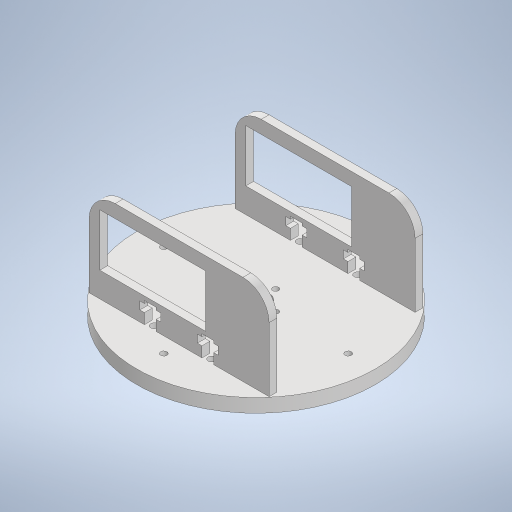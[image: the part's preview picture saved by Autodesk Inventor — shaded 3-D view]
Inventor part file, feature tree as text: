
AUTODESK INVENTOR PART (.ipt)
format: ipt  version: 2023 (Build 270158000, 158)  size: 415,744 bytes
history: native  units: mm
features: extrude x11, sketch x11, pattern_circular x2, mirror x2, other x1, fillet x1
ambient origin geometry x8: Origin, YZ Plane, XZ Plane, XY Plane, X Axis, Y Axis, Z Axis, Center Point
bodies: Body1 (feature_tree)
feature tree (28):
  other  "Sólido1"
  extrude  "Extrusión1"  Depth=5.2mm TaperAngle=0.0deg
  extrude  "Extrusión2"  Depth=2.46mm
  pattern_circular  "Patrón circular1"  Count=4 Angle=360.0deg
  extrude  "Extrusión3"  Depth=11.0mm
  extrude  "Extrusión4"  Depth=7.2mm
  extrude  "Extrusión5"  Depth=2.8mm
  fillet  "Empalme1"  Radius=2.8mm
  extrude  "Extrusión6"  Depth=68.8mm
  mirror  "Simetría1"
  mirror  "Simetría2"
  extrude  "Extrusión7"  Depth=3.0mm TaperAngle=0.0deg
  extrude  "Extrusión8"  Depth=10.0mm
  pattern_circular  "Patrón circular2"  [2 undecoded]
  extrude  "Extrusión9"  Depth=10.0mm
  extrude  "Extrusión10"  Depth=10.0mm TaperAngle=0.0deg
  extrude  "Extrusión11"  Depth=10.0mm
  sketch  "Boceto1"  dims[d0=91.1mm d1=5.2mm d2=0.0mm]
  sketch  "Boceto2"  dims[d3=70.5mm d4=2.46mm]
  sketch  "Boceto3"  dims[d5=5.2mm d6=0.0mm d7=40.0mm d8=360.0deg]
  sketch  "Boceto4"  dims[d11=27.9mm d12=11.0mm]
  sketch  "Boceto5"  dims[d13=7.2mm d14=7.2mm]
  sketch  "Boceto6"  dims[d15=2.6mm d16=0.0mm d17=2.8mm d18=2.8mm]
  sketch  "Boceto7"  dims[d19=2.6mm d20=0.0mm d21=68.8mm]
  sketch  "Boceto8"  dims[d22=3.0mm d23=34.5mm d24=0.0mm]
  sketch  "Boceto9"  dims[d25=10.0mm d26=8.0mm]
  sketch  "Boceto10"  dims[d27=4.5mm]
  sketch  "Boceto11"  dims[d28=3.0mm d29=7.0mm d30=8.0mm d31=34.5mm d32=0.0mm d33=4.5mm d34=9.7mm d35=10.0mm d36=0.0mm d37=15.0mm d38=2.3mm d39=10.0mm d40=0.0mm d41=40.0mm d42=360.0deg d44=0.5mm d45=0.0mm d46=5.0mm d47=15.0mm d48=15.0mm d49=10.0mm d50=0.0mm d51=40.4mm d52=20.0mm d53=5.0mm d54=10.0mm d55=0.0mm]
note: 2 required parameter values undecoded (feature->parameter linkage not recoverable at this tier; creation-order binding heuristic only, values carry confidence <= 0.55)
